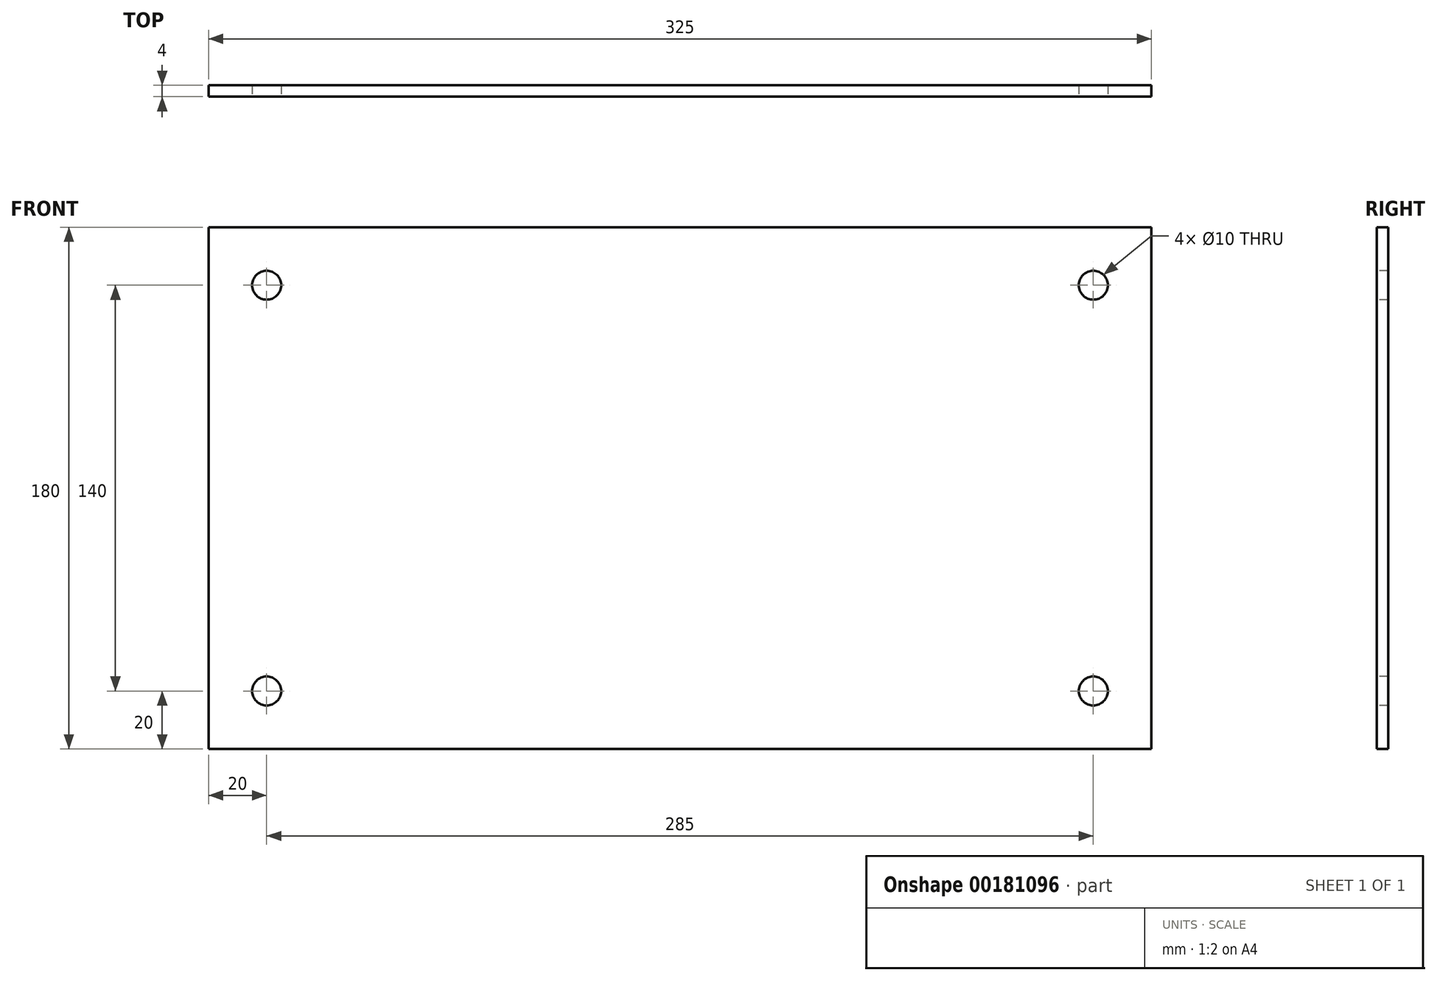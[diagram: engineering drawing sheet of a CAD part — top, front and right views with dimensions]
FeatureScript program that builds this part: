
annotation { "Feature Type Name" : "Feature", "Feature Type Description" : "" }
export const myFeature = defineFeature(function(context is Context, id is Id, definition is map)
    precondition{}
    {
        {
            var Q0;
            Q0=qCreatedBy(makeId("Front.planeOp"),FACE);
            var sketch = newSketch(context, id + "F2", { "sketchPlane" : qUnion([Q0])});
            skLineSegment(sketch, "E0.bottom", {"start": v(162.5, 90) * mm, "end": v(-162.5, 90) * mm});
            skLineSegment(sketch, "E0.top", {"start": v(162.5, -90) * mm, "end": v(-162.5, -90) * mm});
            skLineSegment(sketch, "E0.left", {"start": v(162.5, 90) * mm, "end": v(162.5, -90) * mm});
            skLineSegment(sketch, "E0.right", {"start": v(-162.5, 90) * mm, "end": v(-162.5, -90) * mm});
            skPoint(sketch, "E0.middle", {"position": v(0, 0) * mm});
            skSolve(sketch);
        }
        {
            var Q0;
            Q0 = qSketchRegion(id + "F2", true);
            extrude(context, id + "F3", {"entities" : qUnion([Q0]), "depth" : 4 * mm});
        }
        {
            var Q0;
            Q0=makeQuery(id+"F3.opExtrude","CAP_FACE",FACE,{"disambiguationData":[OSD([sQuery(id+"F2.wireOp",EDGE,"E0.bottom"),sQuery(id+"F2.wireOp",EDGE,"E0.top"),sQuery(id+"F2.wireOp",EDGE,"E0.left"),sQuery(id+"F2.wireOp",EDGE,"E0.right")])],"isStart":false});
            var sketch = newSketch(context, id + "F0", { "sketchPlane" : qUnion([Q0])});
            skLineSegment(sketch, "E1.0", {"start": v(162.5, 90) * mm, "end": v(-162.5, 90) * mm});
            skLineSegment(sketch, "E2.0", {"start": v(-162.5, 90) * mm, "end": v(-162.5, -90) * mm});
            skLineSegment(sketch, "E3.0", {"start": v(162.5, -90) * mm, "end": v(-162.5, -90) * mm});
            skLineSegment(sketch, "E4.0", {"start": v(162.5, 90) * mm, "end": v(162.5, -90) * mm});
            skPoint(sketch, "E5", {"position": v(-142.5, 70) * mm});
            skPoint(sketch, "E6", {"position": v(142.5, 70) * mm});
            skPoint(sketch, "E7", {"position": v(142.5, -70) * mm});
            skPoint(sketch, "E8", {"position": v(-142.5, -70) * mm});
            skSolve(sketch);
        }
        {
            var Q0;
            Q0=sQuery(id+"F0.wireOp",VERTEX,"E5");
            var Q1;
            Q1=sQuery(id+"F0.wireOp",VERTEX,"E8");
            var Q2;
            Q2=sQuery(id+"F0.wireOp",VERTEX,"E6");
            var Q3;
            Q3=sQuery(id+"F0.wireOp",VERTEX,"E7");
            var Q4;
            Q4=makeQuery(id+"F3.opExtrude","SWEPT_BODY",BODY,{"disambiguationData":[OSD([sQuery(id+"F2.wireOp",EDGE,"E0.bottom"),sQuery(id+"F2.wireOp",EDGE,"E0.top"),sQuery(id+"F2.wireOp",EDGE,"E0.left"),sQuery(id+"F2.wireOp",EDGE,"E0.right")])]});
            hole(context, id + "F1", {"style" : HoleStyle.SIMPLE, "endStyle" : HoleEndStyle.THROUGH, "holeDiameter" : 10 * mm, "locations" : qUnion([Q0, Q1, Q2, Q3]), "scope" : qUnion([Q4]), "isTappedThrough" : true});
        }
    });
